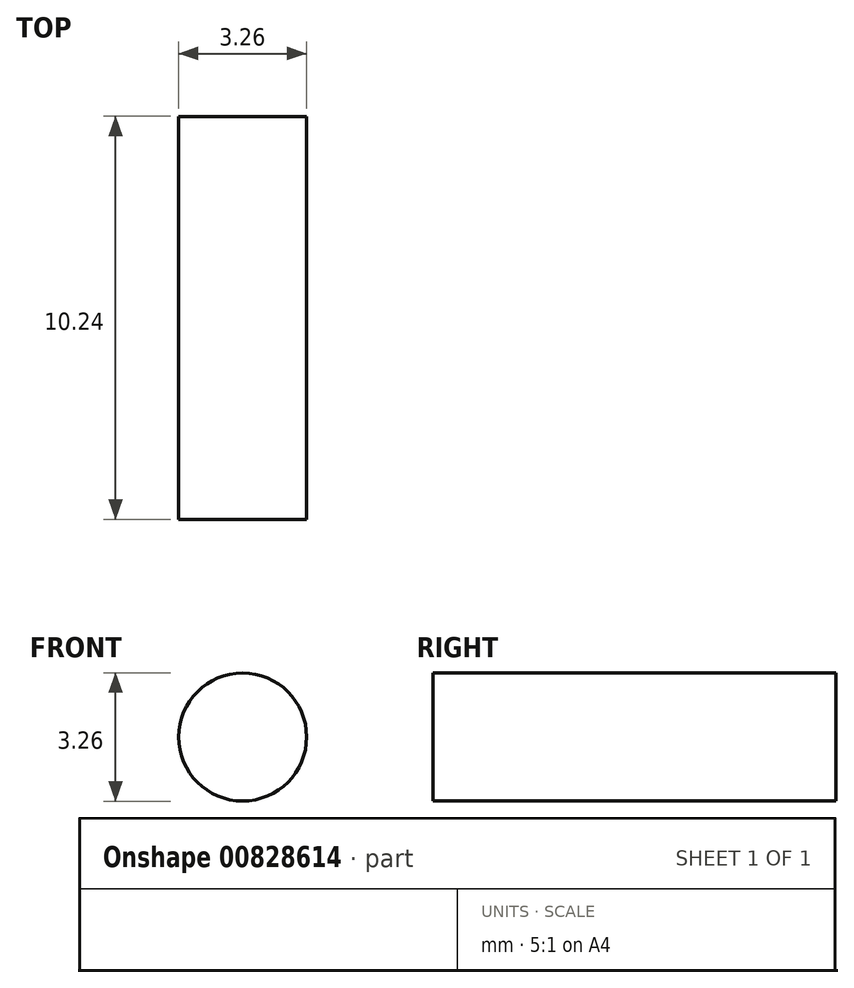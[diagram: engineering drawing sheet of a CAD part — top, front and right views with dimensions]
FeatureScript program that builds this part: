
annotation { "Feature Type Name" : "Feature", "Feature Type Description" : "" }
export const myFeature = defineFeature(function(context is Context, id is Id, definition is map)
    precondition{}
    {
        {
            var Q0;
            Q0=qCreatedBy(makeId("Front.planeOp"),FACE);
            var sketch = newSketch(context, id + "F0", { "sketchPlane" : qUnion([Q0])});
            skCircle(sketch, "E0", {"center": v(0, 0) * mm, "radius": 1.63 * mm});
            skSolve(sketch);
        }
        {
            var Q0;
            Q0=makeQuery(id+"F0.imprint","IMPRINT",FACE,{"disambiguationData":[TD([[makeQuery(id+"F0.imprint","IMPRINT",EDGE,{"derivedFrom":sQuery(id+"F0.wireOp",EDGE,"E0")}),1.0]])]});
            extrude(context, id + "F1", {"entities" : qUnion([Q0]), "endBound" : BoundingType.SYMMETRIC, "depth" : 10.24 * mm, "offsetDistance" : 25.4 * mm});
        }
    });
